# Revit family: 3-751-xx Icon Wall Sconce
name_source: partatom
category: Luminarias
units: mm (PartAtom-declared; Revit-internal decimal feet)

## family parameters
Anfitrión = Muro
Compartido = No
Corte con vacíos al cargar = No
Cota de conector redondo = Diámetro de uso
Número OmniClass = 23.80.70.00
Origen de luz = Sí
Punto de cálculo de habitación = No
Siempre vertical = Sí
Tipo de pieza = Normal
Título OmniClass = Lighting

## types (4) — shared parameters
Cambio de temperatura de color de luz atenuada = <Ninguno>
Comentarios de vataje = 1 x 12.0 W at 120 V
Diffuser = Matte White Acrylic
Fabricante = Oxygen Lighting and Fans
Filtro de color = 16777215
Lámpara = LED Array
Modelo = 3-751-xx / Icon Wall Sconce
References = Ref. 3 = 120 V / Ref. 37 = 277 V
Tamaño de símbolo de origen de luz = 610 mm
URL = www.oxygenlighting.com
Voltage = 120 V
Voltage Input = 120 V or 277 V - 50/60 Hz
zero-valued in all types: Elevación por defecto

## per-type parameters (varying)
| type | Metal Finish 1 |
| 3-751-24 / Satin Nickel - Matte White Acrylic | 24 - Satin Nickel |
| 3-751-14 / Polished Chrome - Matte White Acrylic | 14 - Polished Chrome |
| 3-751-15 / Black - Matte White Acrylic | 15 - Black |
| 3-751-40 / Aged Brass - Matte White Acrylic | 40 - Aged Brass |

## geometry (parser evidence)
native form markers: Sweep x5
no freeform markers — native parametric forms only
